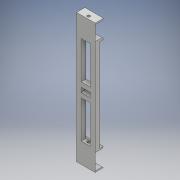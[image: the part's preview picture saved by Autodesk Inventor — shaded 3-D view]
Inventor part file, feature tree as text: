
AUTODESK INVENTOR PART (.ipt)
format: ipt  version: 2018 (Build 220112000, 112)  size: 445,440 bytes
history: native  units: mm
features: extrude x7, sketch x7, chamfer x5
ambient origin geometry x8: Origin, YZ Plane, XZ Plane, XY Plane, X Axis, Y Axis, Z Axis, Center Point
bodies: Solid1 (feature_tree)
feature tree (19):
  extrude  "Extrusion1"  Depth=140.0mm
  extrude  "Extrusion2"  Depth=20.0mm
  extrude  "Extrusion3"  Depth=4.0mm TaperAngle=0.0deg
  extrude  "Extrusion4"  Depth=10.0mm
  extrude  "Extrusion5"  Depth=10.0mm
  chamfer  "Chamfer1"  Distance=5.0mm
  chamfer  "Chamfer2"  Distance=50.0mm
  chamfer  "Chamfer3"  Distance=2.0mm
  extrude  "Extrusion8"  Depth=10.0mm
  extrude  "Extrusion9"  Depth=10.0mm
  chamfer  "Chamfer4"  Distance=5.0mm
  chamfer  "Chamfer5"  Distance=5.0mm
  sketch  "Sketch1"  dims[d0=20.0mm d1=140.0mm]
  sketch  "Sketch2"  dims[d2=5.0mm d3=0.0mm d4=20.0mm]
  sketch  "Sketch3"  dims[d5=20.0mm d6=4.0mm d7=0.0mm]
  sketch  "Sketch4"  dims[d8=5.0mm d9=10.0mm]
  sketch  "Sketch5"  dims[d10=5.0mm d11=10.0mm d12=5.0mm d13=0.0mm d15=50.0mm d16=0.0mm]
  sketch  "Sketch8"  dims[d17=2.0mm]
  sketch  "Sketch9"  dims[d18=5.0mm d19=2.0mm d21=5.0mm d22=2.5mm d23=5.0mm d24=5.0mm d25=5.0mm d26=10.0mm d27=0.0mm d28=4.0mm d29=2.0mm d30=45.0deg d31=5.0mm d32=2.0mm d33=45.0deg d34=3.5mm d35=2.0mm d36=45.0deg d46=2.0mm d53=3.0mm d54=3.0mm d55=30.0mm d56=0.0mm d57=5.0mm d58=30.0mm d59=0.0mm d60=2.0mm d61=3.0mm d62=2.0mm d63=45.0deg d64=3.0mm d65=2.0mm d66=45.0deg]
